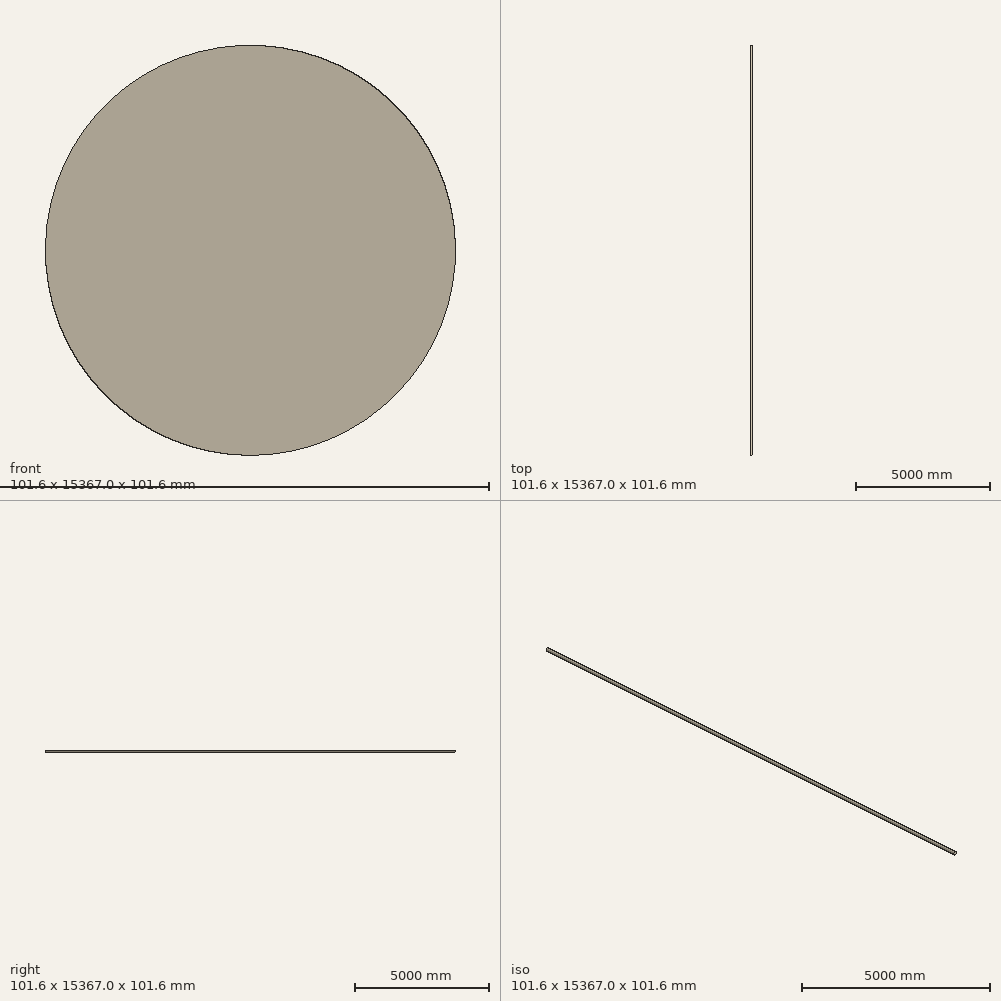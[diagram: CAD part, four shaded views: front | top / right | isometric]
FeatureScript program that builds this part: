
annotation { "Feature Type Name" : "Feature", "Feature Type Description" : "" }
export const myFeature = defineFeature(function(context is Context, id is Id, definition is map)
    precondition{}
    {
        {
            var Q0;
            Q0=qCreatedBy(makeId("Front.planeOp"),FACE);
            var sketch = newSketch(context, id + "F0", { "sketchPlane" : qUnion([Q0])});
            skCircle(sketch, "E0", {"center": v(0, 0) * mm, "radius": 50.8 * mm});
            skSolve(sketch);
        }
        {
            var Q0;
            Q0 = qSketchRegion(id + "F0", true);
            extrude(context, id + "F1", {"entities" : qUnion([Q0]), "depth" : 15367 * mm, "offsetDistance" : 25.4 * mm});
        }
    });
